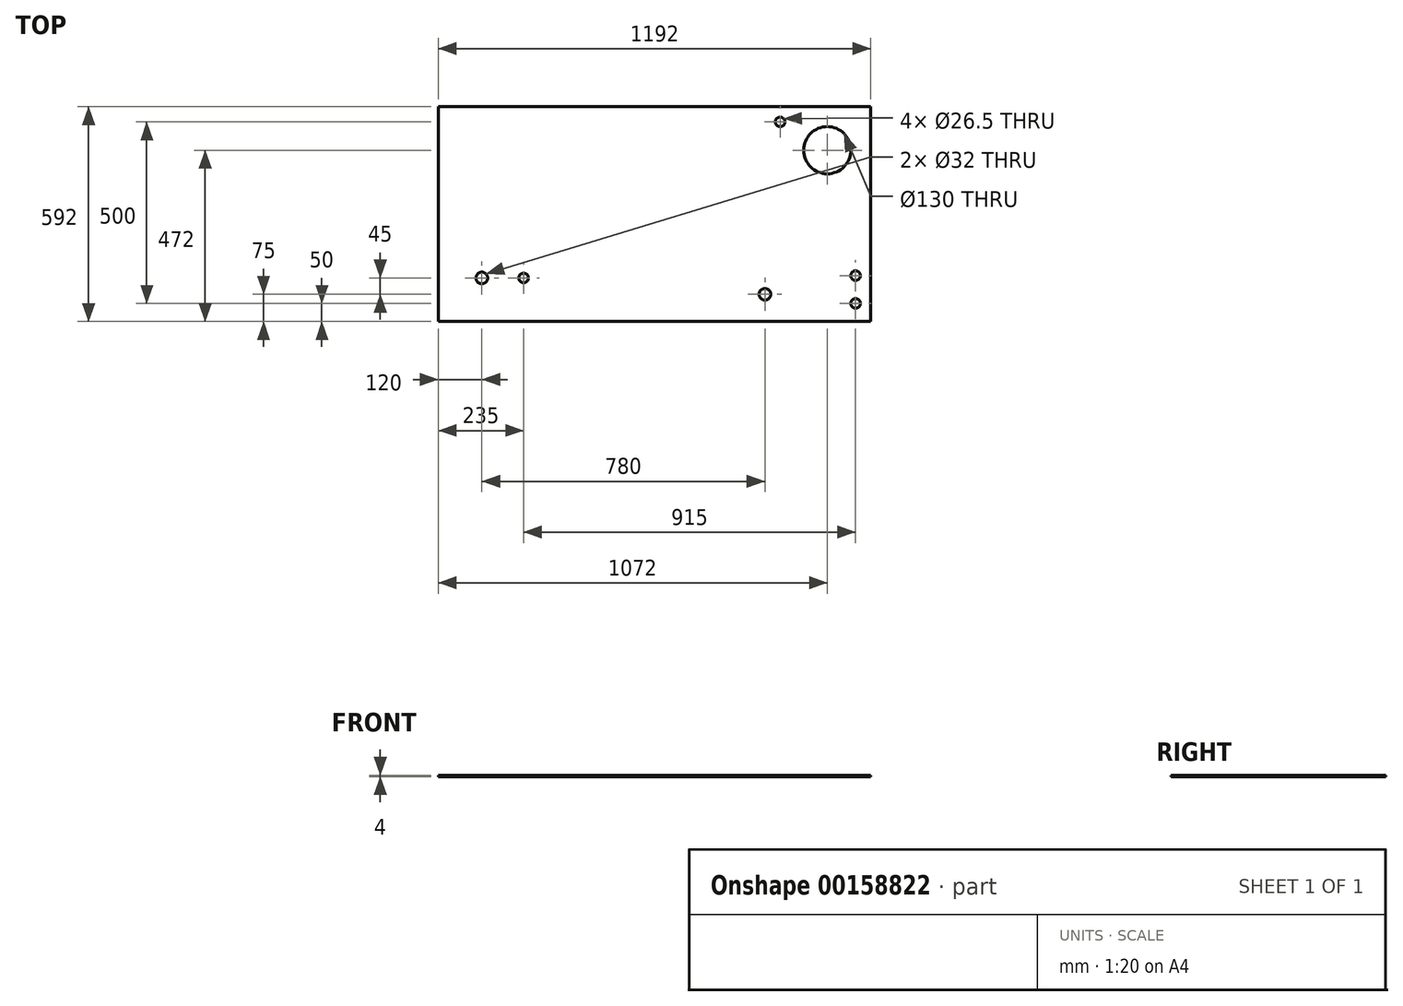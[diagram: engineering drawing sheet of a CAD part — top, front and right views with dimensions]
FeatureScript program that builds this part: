
annotation { "Feature Type Name" : "Feature", "Feature Type Description" : "" }
export const myFeature = defineFeature(function(context is Context, id is Id, definition is map)
    precondition{}
    {
        {
            var Q0;
            Q0=qCreatedBy(makeId("Top.planeOp"),FACE);
            var sketch = newSketch(context, id + "F0", { "sketchPlane" : qUnion([Q0])});
            skCircle(sketch, "E0", {"center": v(1072, 472) * mm, "radius": 65 * mm});
            skCircle(sketch, "E1", {"center": v(942, 550) * mm, "radius": 13.25 * mm});
            skCircle(sketch, "E2", {"center": v(1150, 126.5) * mm, "radius": 13.25 * mm});
            skCircle(sketch, "E3", {"center": v(1150, 50) * mm, "radius": 13.25 * mm});
            skCircle(sketch, "E4", {"center": v(900, 75) * mm, "radius": 16 * mm});
            skCircle(sketch, "E5", {"center": v(235, 120) * mm, "radius": 13.25 * mm});
            skCircle(sketch, "E6", {"center": v(120, 120) * mm, "radius": 16 * mm});
            skLineSegment(sketch, "E7.bottom", {"start": v(0, 592) * mm, "end": v(1192, 592) * mm});
            skLineSegment(sketch, "E7.top", {"start": v(0, 0) * mm, "end": v(1192, 0) * mm});
            skLineSegment(sketch, "E7.left", {"start": v(0, 592) * mm, "end": v(0, 0) * mm});
            skLineSegment(sketch, "E7.right", {"start": v(1192, 592) * mm, "end": v(1192, 0) * mm});
            skSolve(sketch);
        }
        {
            var Q0;
            Q0 = qSketchRegion(id + "F0", true);
            extrude(context, id + "F1", {"entities" : qUnion([Q0]), "depth" : 4 * mm});
        }
    });
